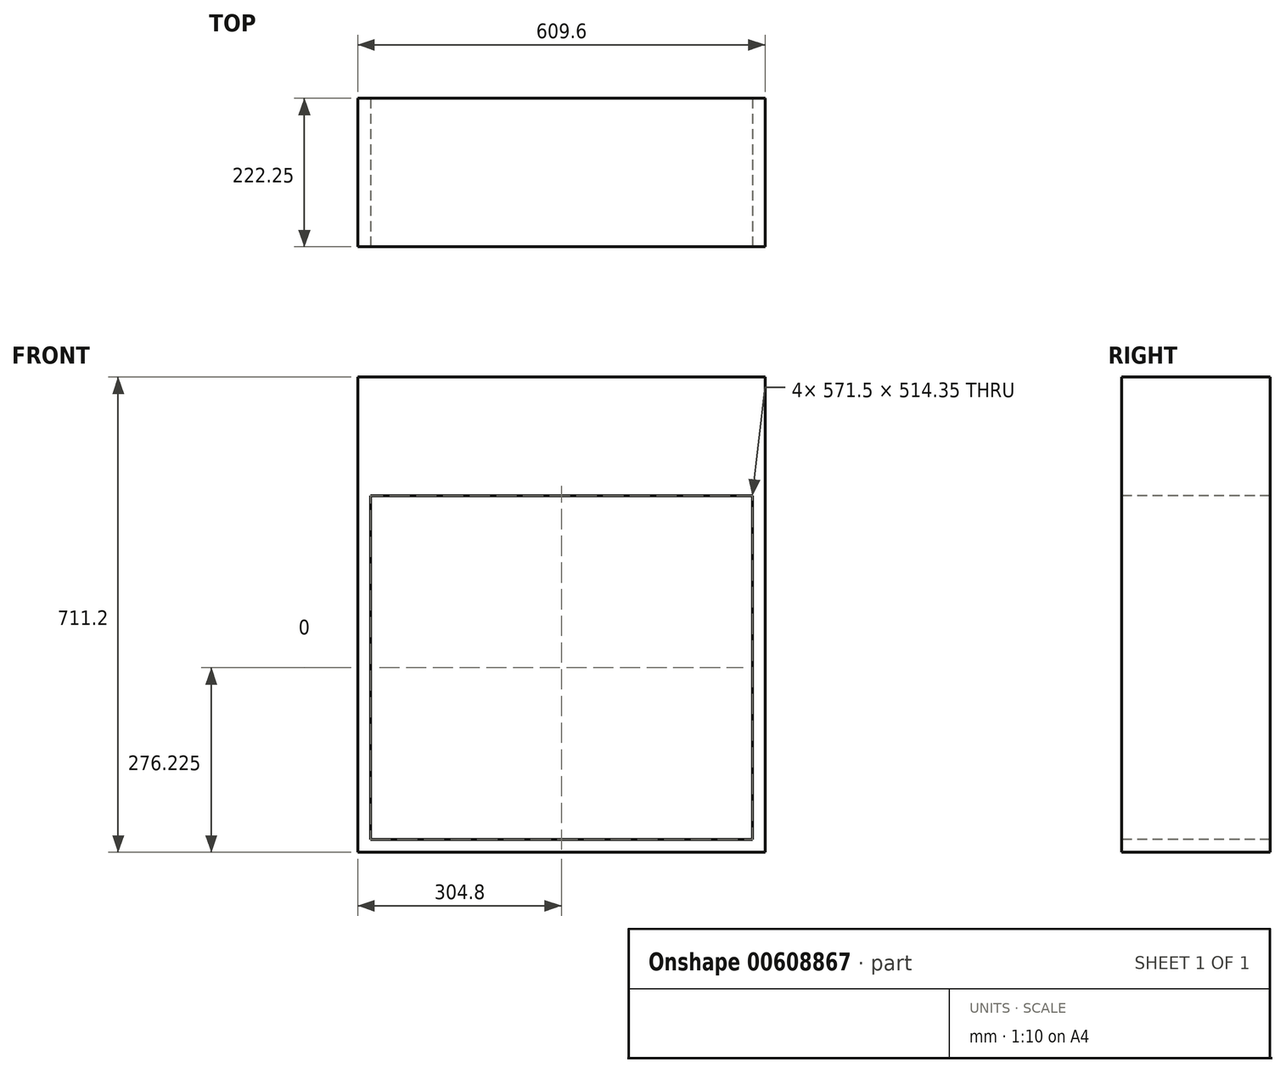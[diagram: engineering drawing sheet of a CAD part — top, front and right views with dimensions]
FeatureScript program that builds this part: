
annotation { "Feature Type Name" : "Feature", "Feature Type Description" : "" }
export const myFeature = defineFeature(function(context is Context, id is Id, definition is map)
    precondition{}
    {
        {
            var Q0;
            Q0=qCreatedBy(makeId("Right.planeOp"),FACE);
            var sketch = newSketch(context, id + "F0", { "sketchPlane" : qUnion([Q0])});
            skLineSegment(sketch, "E0.bottom", {"start": v(222.25, 0) * mm, "end": v(0, 0) * mm});
            skLineSegment(sketch, "E0.top", {"start": v(222.25, 711.2) * mm, "end": v(0, 711.2) * mm});
            skLineSegment(sketch, "E0.left", {"start": v(0, 0) * mm, "end": v(0, 711.2) * mm});
            skLineSegment(sketch, "E0.right", {"start": v(222.25, 0) * mm, "end": v(222.25, 711.2) * mm});
            skSolve(sketch);
        }
        {
            var Q0;
            Q0=makeQuery(id+"F0.imprint","IMPRINT",FACE,{"disambiguationData":[TD([[makeQuery(id+"F0.imprint","IMPRINT",EDGE,{"derivedFrom":sQuery(id+"F0.wireOp",EDGE,"E0.bottom")}),-1.0]])]});
            extrude(context, id + "F1", {"entities" : qUnion([Q0]), "oppositeDirection" : true, "depth" : 609.6 * mm, "offsetDistance" : 25.4 * mm});
        }
        {
            var Q0;
            Q0=makeQuery(id+"F1.opExtrude","SWEPT_FACE",FACE,{"disambiguationData":[OSD([sQuery(id+"F0.wireOp",EDGE,"E0.left")])]});
            var sketch = newSketch(context, id + "F2", { "sketchPlane" : qUnion([Q0])});
            skLineSegment(sketch, "E1.bottom", {"start": v(-590.55, 19.05) * mm, "end": v(-19.05, 19.05) * mm});
            skLineSegment(sketch, "E1.top", {"start": v(-590.55, 533.4) * mm, "end": v(-19.05, 533.4) * mm});
            skLineSegment(sketch, "E1.left", {"start": v(-590.55, 19.05) * mm, "end": v(-590.55, 533.4) * mm});
            skLineSegment(sketch, "E1.right", {"start": v(-19.05, 19.05) * mm, "end": v(-19.05, 533.4) * mm});
            skSolve(sketch);
        }
        {
            var Q0;
            Q0 = qSketchRegion(id + "F2", true);
            extrude(context, id + "F3", {"entities" : qUnion([Q0]), "operationType" : NewBodyOperationType.REMOVE, "oppositeDirection" : true, "depth" : 285.75 * mm, "offsetDistance" : 25.4 * mm});
        }
        {
            var Q0;
            Q0=makeQuery(id+"F3.boolean.opBoolean","COPY",FACE,{"derivedFrom":makeQuery(id+"F3.opExtrude","SWEPT_FACE",FACE,{"disambiguationData":[OSD([sQuery(id+"F2.wireOp",EDGE,"E1.top")])]})});
            var sketch = newSketch(context, id + "F4", { "sketchPlane" : qUnion([Q0])});
            skLineSegment(sketch, "E2.bottom", {"start": v(-590.55, -285.75) * mm, "end": v(-19.05, -285.75) * mm});
            skLineSegment(sketch, "E2.top", {"start": v(-590.55, -19.05) * mm, "end": v(-19.05, -19.05) * mm});
            skLineSegment(sketch, "E2.left", {"start": v(-590.55, -285.75) * mm, "end": v(-590.55, -19.05) * mm});
            skLineSegment(sketch, "E2.right", {"start": v(-19.05, -285.75) * mm, "end": v(-19.05, -19.05) * mm});
            skSolve(sketch);
        }
        {
            var Q0;
            Q0=makeQuery(id+"F4.imprint","IMPRINT",FACE,{"disambiguationData":[TD([[makeQuery(id+"F4.imprint","IMPRINT",EDGE,{"derivedFrom":sQuery(id+"F4.wireOp",EDGE,"E2.bottom")}),1.0]])]});
            extrude(context, id + "F5", {"entities" : qUnion([Q0]), "operationType" : NewBodyOperationType.REMOVE, "oppositeDirection" : true, "depth" : 158.75 * mm, "offsetDistance" : 25.4 * mm});
        }
    });
